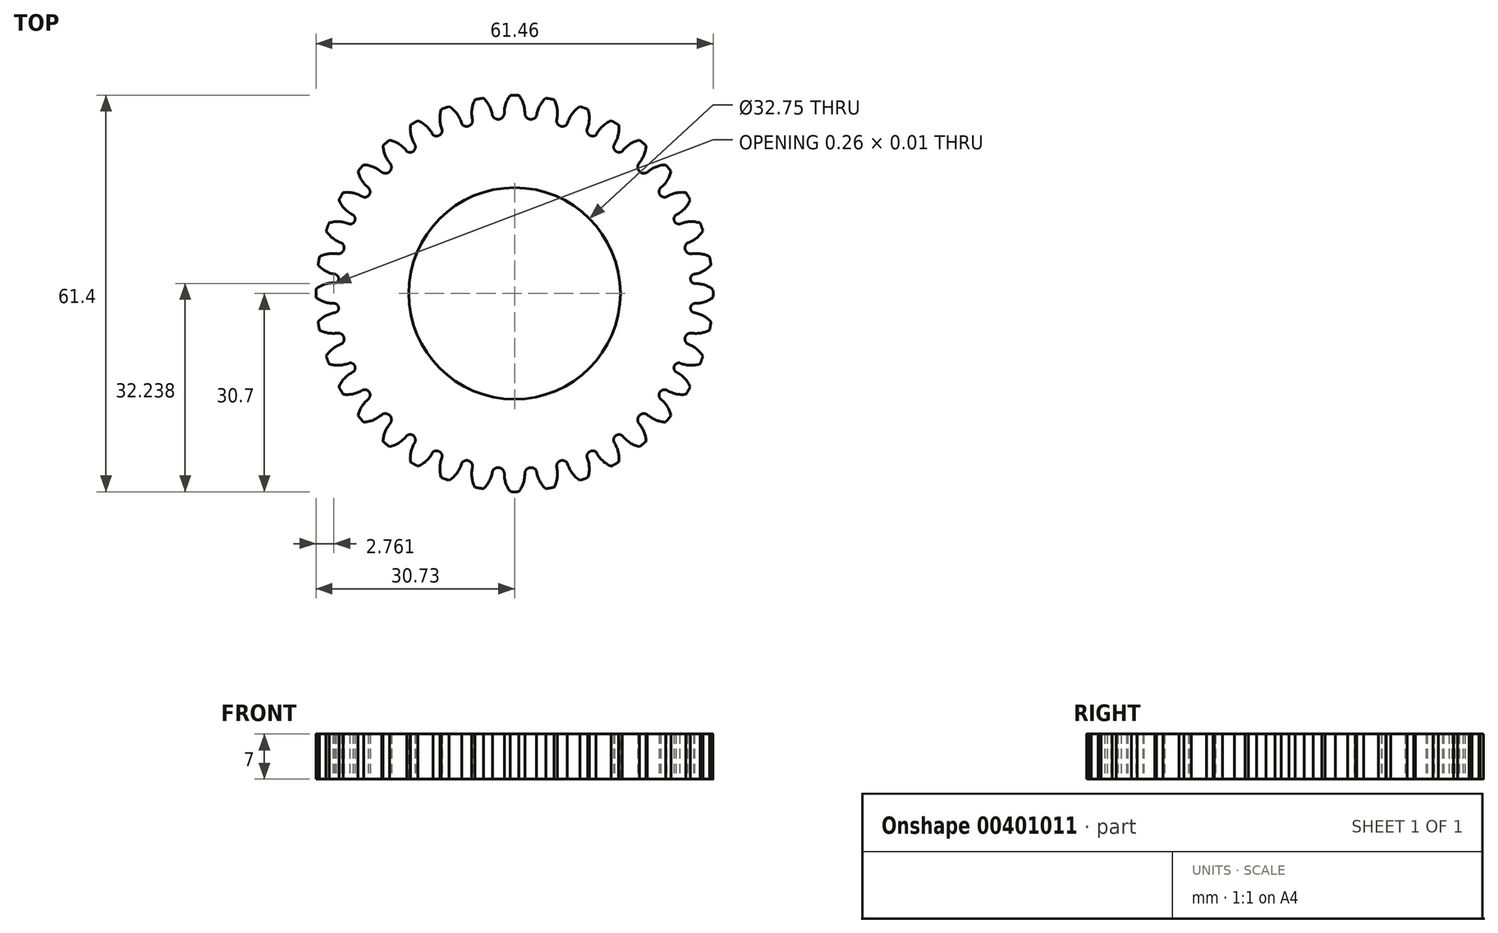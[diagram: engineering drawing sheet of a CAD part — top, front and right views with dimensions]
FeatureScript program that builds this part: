
annotation { "Feature Type Name" : "Feature", "Feature Type Description" : "" }
export const myFeature = defineFeature(function(context is Context, id is Id, definition is map)
    precondition{}
    {
        {
            var Q0;
            Q0=qCreatedBy(makeId("Top.planeOp"),FACE);
            var sketch = newSketch(context, id + "F0", { "sketchPlane" : qUnion([Q0])});
            skArc(sketch, "E0", {"start": v(0.66, 30.69) * mm, "mid": v(0, 30.7) * mm, "end": v(-0.66, 30.69) * mm});
            skLineSegment(sketch, "E1", {"start": v(-1.54, 28.62) * mm, "end": v(-0.66, 30.69) * mm, "construction": true});
            skArc(sketch, "E2", {"start": v(-0.66, 30.69) * mm, "mid": v(-1.56, 28.5) * mm, "end": v(-1.2, 26.14) * mm});
            skArc(sketch, "E3", {"start": v(1.2, 26.14) * mm, "mid": v(1.56, 28.5) * mm, "end": v(0.66, 30.69) * mm});
            skLineSegment(sketch, "E4.MirrorCS", {"start": v(-1.54, -28.62) * mm, "end": v(-0.66, -30.69) * mm, "construction": true});
            skArc(sketch, "E5.MirrorCS", {"start": v(1.2, -26.14) * mm, "mid": v(1.56, -28.5) * mm, "end": v(0.66, -30.69) * mm});
            skArc(sketch, "E6.MirrorCS", {"start": v(0.66, -30.69) * mm, "mid": v(0, -30.7) * mm, "end": v(-0.66, -30.69) * mm});
            skArc(sketch, "E7.MirrorCS", {"start": v(-0.66, -30.69) * mm, "mid": v(-1.56, -28.5) * mm, "end": v(-1.2, -26.14) * mm});
            skArc(sketch, "E8", {"start": v(-30.72, 0.61) * mm, "mid": v(-30.73, -0.05) * mm, "end": v(-30.72, -0.7) * mm});
            skLineSegment(sketch, "E9", {"start": v(-28.65, -1.58) * mm, "end": v(-30.72, -0.7) * mm, "construction": true});
            skArc(sketch, "E10", {"start": v(-28.65, -1.58) * mm, "mid": v(-28.14, -1.63) * mm, "end": v(-27.62, -1.62) * mm});
            skArc(sketch, "E11", {"start": v(-27.84, 1.54) * mm, "mid": v(-29.36, 1.33) * mm, "end": v(-30.72, 0.61) * mm});
            skLineSegment(sketch, "E12", {"start": v(-1.54, 28.62) * mm, "end": v(-3.55, 28.42) * mm, "construction": true});
            skArc(sketch, "E13", {"start": v(-4.83, 30.23) * mm, "mid": v(-5.48, 30.13) * mm, "end": v(-6.13, 30) * mm});
            skLineSegment(sketch, "E14", {"start": v(-6.64, 27.81) * mm, "end": v(-6.13, 30) * mm, "construction": true});
            skArc(sketch, "E15", {"start": v(-6.13, 30) * mm, "mid": v(-6.63, 27.68) * mm, "end": v(-5.88, 25.43) * mm});
            skArc(sketch, "E16", {"start": v(-3.5, 25.85) * mm, "mid": v(-3.56, 28.22) * mm, "end": v(-4.83, 30.23) * mm});
            skArc(sketch, "E17", {"start": v(-10.12, 28.94) * mm, "mid": v(-10.74, 28.73) * mm, "end": v(-11.35, 28.5) * mm});
            skLineSegment(sketch, "E18", {"start": v(-11.48, 26.25) * mm, "end": v(-11.35, 28.5) * mm, "construction": true});
            skArc(sketch, "E19", {"start": v(-11.35, 28.5) * mm, "mid": v(-11.45, 26.12) * mm, "end": v(-10.32, 24.03) * mm});
            skArc(sketch, "E20", {"start": v(-8.05, 24.86) * mm, "mid": v(-8.52, 27.19) * mm, "end": v(-10.12, 28.94) * mm});
            skArc(sketch, "E21", {"start": v(-14.96, 26.75) * mm, "mid": v(-15.54, 26.43) * mm, "end": v(-16.1, 26.09) * mm});
            skLineSegment(sketch, "E22", {"start": v(-15.83, 23.86) * mm, "end": v(-16.1, 26.09) * mm, "construction": true});
            skArc(sketch, "E23", {"start": v(-16.1, 26.09) * mm, "mid": v(-15.78, 23.74) * mm, "end": v(-14.3, 21.88) * mm});
            skArc(sketch, "E24", {"start": v(-12.2, 23.09) * mm, "mid": v(-13.08, 25.3) * mm, "end": v(-14.96, 26.75) * mm});
            skArc(sketch, "E25", {"start": v(-19.34, 23.74) * mm, "mid": v(-19.85, 23.33) * mm, "end": v(-20.35, 22.9) * mm});
            skLineSegment(sketch, "E26", {"start": v(-19.7, 20.75) * mm, "end": v(-20.35, 22.9) * mm, "construction": true});
            skArc(sketch, "E27", {"start": v(-20.35, 22.9) * mm, "mid": v(-19.62, 20.64) * mm, "end": v(-17.85, 19.06) * mm});
            skArc(sketch, "E28", {"start": v(-16, 20.61) * mm, "mid": v(-17.24, 22.64) * mm, "end": v(-19.34, 23.74) * mm});
            skArc(sketch, "E29", {"start": v(-23.36, 19.91) * mm, "mid": v(-23.8, 19.42) * mm, "end": v(-24.2, 18.9) * mm});
            skLineSegment(sketch, "E30", {"start": v(-23.2, 16.9) * mm, "end": v(-24.2, 18.9) * mm, "construction": true});
            skArc(sketch, "E31", {"start": v(-24.2, 18.9) * mm, "mid": v(-23.64, 17.5) * mm, "end": v(-22.64, 16.37) * mm});
            skArc(sketch, "E32", {"start": v(-19.53, 17.42) * mm, "mid": v(-21.1, 19.2) * mm, "end": v(-23.36, 19.91) * mm});
            skArc(sketch, "E33", {"start": v(-26.52, 15.62) * mm, "mid": v(-26.86, 15.06) * mm, "end": v(-27.18, 14.48) * mm});
            skLineSegment(sketch, "E34", {"start": v(-25.83, 12.68) * mm, "end": v(-27.18, 14.48) * mm, "construction": true});
            skArc(sketch, "E35", {"start": v(-27.18, 14.48) * mm, "mid": v(-26.3, 13.11) * mm, "end": v(-24.98, 12.15) * mm});
            skArc(sketch, "E36", {"start": v(-23.5, 14.94) * mm, "mid": v(-24.95, 15.55) * mm, "end": v(-26.52, 15.62) * mm});
            skArc(sketch, "E37", {"start": v(-28.7, 10.92) * mm, "mid": v(-28.94, 10.3) * mm, "end": v(-29.16, 9.68) * mm});
            skLineSegment(sketch, "E38", {"start": v(-27.52, 8.14) * mm, "end": v(-29.16, 9.68) * mm, "construction": true});
            skArc(sketch, "E39", {"start": v(-29.16, 9.68) * mm, "mid": v(-28.13, 8.55) * mm, "end": v(-26.79, 7.83) * mm});
            skArc(sketch, "E40", {"start": v(-30.18, 5.68) * mm, "mid": v(-30.3, 5.03) * mm, "end": v(-30.4, 4.38) * mm});
            skLineSegment(sketch, "E41", {"start": v(-28.52, 3.16) * mm, "end": v(-30.4, 4.38) * mm, "construction": true});
            skArc(sketch, "E42", {"start": v(-30.4, 4.38) * mm, "mid": v(-28.4, 3.12) * mm, "end": v(-26.02, 3.05) * mm});
            skArc(sketch, "E43", {"start": v(-25.6, 5.43) * mm, "mid": v(-27.86, 6.18) * mm, "end": v(-30.18, 5.68) * mm});
            skArc(sketch, "E44", {"start": v(-28.1, 1.54) * mm, "mid": v(-27.23, 2.21) * mm, "end": v(-27.98, 3.01) * mm});
            skArc(sketch, "E45", {"start": v(-27.43, 6.14) * mm, "mid": v(-26.43, 6.73) * mm, "end": v(-26.79, 7.83) * mm});
            skArc(sketch, "E46", {"start": v(-25.93, 10.9) * mm, "mid": v(-24.76, 11.16) * mm, "end": v(-25.21, 12.27) * mm});
            skArc(sketch, "E47", {"start": v(-23.77, 15.1) * mm, "mid": v(-22.54, 15.2) * mm, "end": v(-22.7, 16.42) * mm});
            skArc(sketch, "E48", {"start": v(-20.72, 18.92) * mm, "mid": v(-19.37, 18.84) * mm, "end": v(-19.3, 20.2) * mm});
            skArc(sketch, "E49", {"start": v(-16.93, 22.32) * mm, "mid": v(-15.79, 21.93) * mm, "end": v(-15.44, 23.08) * mm});
            skArc(sketch, "E50", {"start": v(-12.98, 25.15) * mm, "mid": v(-11.77, 24.42) * mm, "end": v(-11.35, 25.77) * mm});
            skArc(sketch, "E51", {"start": v(-8.33, 26.75) * mm, "mid": v(-7.21, 25.88) * mm, "end": v(-6.57, 27.13) * mm});
            skArc(sketch, "E52", {"start": v(-3.49, 27.95) * mm, "mid": v(-2.54, 26.96) * mm, "end": v(-1.59, 27.95) * mm});
            skArc(sketch, "E53.MirrorCS", {"start": v(4.83, 30.23) * mm, "mid": v(5.48, 30.13) * mm, "end": v(6.13, 30) * mm});
            skArc(sketch, "E54.MirrorCS", {"start": v(20.72, 18.92) * mm, "mid": v(19.37, 18.84) * mm, "end": v(19.3, 20.2) * mm});
            skArc(sketch, "E55.MirrorCS", {"start": v(30.18, 5.68) * mm, "mid": v(30.3, 5.03) * mm, "end": v(30.4, 4.38) * mm});
            skArc(sketch, "E56.MirrorCS", {"start": v(30.72, 0.61) * mm, "mid": v(30.73, -0.05) * mm, "end": v(30.72, -0.7) * mm});
            skLineSegment(sketch, "E57.MirrorCS", {"start": v(25.83, 12.68) * mm, "end": v(27.18, 14.48) * mm, "construction": true});
            skArc(sketch, "E58.MirrorCS", {"start": v(14.96, 26.75) * mm, "mid": v(15.54, 26.43) * mm, "end": v(16.1, 26.09) * mm});
            skArc(sketch, "E59.MirrorCS", {"start": v(23.36, 19.91) * mm, "mid": v(23.8, 19.42) * mm, "end": v(24.2, 18.9) * mm});
            skArc(sketch, "E60.MirrorCS", {"start": v(12.98, 25.15) * mm, "mid": v(11.77, 24.42) * mm, "end": v(11.35, 25.77) * mm});
            skArc(sketch, "E61.MirrorCS", {"start": v(11.35, 28.5) * mm, "mid": v(11.45, 26.12) * mm, "end": v(10.32, 24.03) * mm});
            skLineSegment(sketch, "E62.MirrorCS", {"start": v(11.48, 26.25) * mm, "end": v(11.35, 28.5) * mm, "construction": true});
            skArc(sketch, "E63.MirrorCS", {"start": v(19.34, 23.74) * mm, "mid": v(19.85, 23.33) * mm, "end": v(20.35, 22.9) * mm});
            skArc(sketch, "E64.MirrorCS", {"start": v(28.7, 10.92) * mm, "mid": v(28.94, 10.3) * mm, "end": v(29.16, 9.68) * mm});
            skArc(sketch, "E65.MirrorCS", {"start": v(10.12, 28.94) * mm, "mid": v(10.74, 28.73) * mm, "end": v(11.35, 28.5) * mm});
            skLineSegment(sketch, "E66.MirrorCS", {"start": v(23.2, 16.9) * mm, "end": v(24.2, 18.9) * mm, "construction": true});
            skArc(sketch, "E67.MirrorCS", {"start": v(-0.66, 30.69) * mm, "mid": v(0, 30.7) * mm, "end": v(0.66, 30.69) * mm});
            skArc(sketch, "E68.MirrorCS", {"start": v(26.52, 15.62) * mm, "mid": v(26.86, 15.06) * mm, "end": v(27.18, 14.48) * mm});
            skArc(sketch, "E69.MirrorCS", {"start": v(23.77, 15.1) * mm, "mid": v(22.54, 15.2) * mm, "end": v(22.7, 16.42) * mm});
            skArc(sketch, "E70.MirrorCS", {"start": v(25.6, 5.43) * mm, "mid": v(27.86, 6.18) * mm, "end": v(30.18, 5.68) * mm});
            skArc(sketch, "E71.MirrorCS", {"start": v(6.13, 30) * mm, "mid": v(6.63, 27.74) * mm, "end": v(5.94, 25.52) * mm});
            skArc(sketch, "E72.MirrorCS", {"start": v(27.18, 14.48) * mm, "mid": v(25.73, 12.6) * mm, "end": v(23.52, 11.73) * mm});
            skArc(sketch, "E73.MirrorCS", {"start": v(16, 20.61) * mm, "mid": v(17.24, 22.64) * mm, "end": v(19.34, 23.74) * mm});
            skLineSegment(sketch, "E74.MirrorCS", {"start": v(15.83, 23.86) * mm, "end": v(16.1, 26.09) * mm, "construction": true});
            skArc(sketch, "E75.MirrorCS", {"start": v(3.47, 25.97) * mm, "mid": v(3.58, 28.28) * mm, "end": v(4.83, 30.23) * mm});
            skArc(sketch, "E76.MirrorCS", {"start": v(22.3, 13.82) * mm, "mid": v(24.17, 15.3) * mm, "end": v(26.52, 15.62) * mm});
            skArc(sketch, "E77.MirrorCS", {"start": v(16.93, 22.32) * mm, "mid": v(15.79, 21.93) * mm, "end": v(15.44, 23.08) * mm});
            skArc(sketch, "E78.MirrorCS", {"start": v(16.1, 26.09) * mm, "mid": v(15.78, 23.74) * mm, "end": v(14.3, 21.88) * mm});
            skArc(sketch, "E79.MirrorCS", {"start": v(27.43, 6.14) * mm, "mid": v(26.43, 6.73) * mm, "end": v(26.79, 7.83) * mm});
            skArc(sketch, "E80.MirrorCS", {"start": v(0.66, 30.69) * mm, "mid": v(1.56, 28.5) * mm, "end": v(1.2, 26.14) * mm});
            skLineSegment(sketch, "E81.MirrorCS", {"start": v(28.52, 3.16) * mm, "end": v(30.4, 4.38) * mm, "construction": true});
            skArc(sketch, "E82.MirrorCS", {"start": v(26.17, 1.16) * mm, "mid": v(28.52, 1.51) * mm, "end": v(30.72, 0.61) * mm});
            skArc(sketch, "E83.MirrorCS", {"start": v(19.53, 17.42) * mm, "mid": v(21.1, 19.2) * mm, "end": v(23.36, 19.91) * mm});
            skArc(sketch, "E84.MirrorCS", {"start": v(28.1, 1.54) * mm, "mid": v(27.23, 2.21) * mm, "end": v(27.98, 3.01) * mm});
            skArc(sketch, "E85.MirrorCS", {"start": v(24.2, 18.9) * mm, "mid": v(23.1, 16.8) * mm, "end": v(21.08, 15.56) * mm});
            skArc(sketch, "E86.MirrorCS", {"start": v(3.49, 27.95) * mm, "mid": v(2.54, 26.96) * mm, "end": v(1.59, 27.95) * mm});
            skLineSegment(sketch, "E87.MirrorCS", {"start": v(27.52, 8.14) * mm, "end": v(29.16, 9.68) * mm, "construction": true});
            skLineSegment(sketch, "E88.MirrorCS", {"start": v(19.7, 20.75) * mm, "end": v(20.35, 22.9) * mm, "construction": true});
            skArc(sketch, "E89.MirrorCS", {"start": v(29.16, 9.68) * mm, "mid": v(27.4, 8.08) * mm, "end": v(25.07, 7.6) * mm});
            skArc(sketch, "E90.MirrorCS", {"start": v(8.33, 26.75) * mm, "mid": v(7.21, 25.88) * mm, "end": v(6.57, 27.13) * mm});
            skLineSegment(sketch, "E91.MirrorCS", {"start": v(1.54, 28.62) * mm, "end": v(3.55, 28.42) * mm, "construction": true});
            skLineSegment(sketch, "E92.MirrorCS", {"start": v(1.54, 28.62) * mm, "end": v(0.66, 30.69) * mm, "construction": true});
            skArc(sketch, "E93.MirrorCS", {"start": v(30.4, 4.38) * mm, "mid": v(28.4, 3.12) * mm, "end": v(26.02, 3.05) * mm});
            skArc(sketch, "E94.MirrorCS", {"start": v(12.2, 23.09) * mm, "mid": v(13.08, 25.3) * mm, "end": v(14.96, 26.75) * mm});
            skArc(sketch, "E95.MirrorCS", {"start": v(25.93, 10.9) * mm, "mid": v(24.76, 11.16) * mm, "end": v(25.21, 12.27) * mm});
            skLineSegment(sketch, "E96.MirrorCS", {"start": v(6.64, 27.81) * mm, "end": v(6.13, 30) * mm, "construction": true});
            skArc(sketch, "E97.MirrorCS", {"start": v(24.25, 9.88) * mm, "mid": v(26.33, 11) * mm, "end": v(28.7, 10.92) * mm});
            skArc(sketch, "E98.MirrorCS", {"start": v(8.05, 24.86) * mm, "mid": v(8.52, 27.19) * mm, "end": v(10.12, 28.94) * mm});
            skArc(sketch, "E99.MirrorCS", {"start": v(20.35, 22.9) * mm, "mid": v(19.62, 20.64) * mm, "end": v(17.85, 19.06) * mm});
            skLineSegment(sketch, "E100.MirrorCS", {"start": v(28.65, -1.58) * mm, "end": v(30.72, -0.7) * mm, "construction": true});
            skArc(sketch, "E101.MirrorCS", {"start": v(-1.2, 26.14) * mm, "mid": v(-1.56, 28.5) * mm, "end": v(-0.66, 30.69) * mm});
            skArc(sketch, "E102.MirrorCS", {"start": v(-0.66, -30.69) * mm, "mid": v(0, -30.7) * mm, "end": v(0.66, -30.69) * mm});
            skLineSegment(sketch, "E103.MirrorCS", {"start": v(1.54, -28.62) * mm, "end": v(0.66, -30.69) * mm, "construction": true});
            skArc(sketch, "E104.MirrorCS", {"start": v(-1.2, -26.14) * mm, "mid": v(-1.56, -28.5) * mm, "end": v(-0.66, -30.69) * mm});
            skLineSegment(sketch, "E105.MirrorCS", {"start": v(23.2, -16.9) * mm, "end": v(24.2, -18.9) * mm, "construction": true});
            skLineSegment(sketch, "E106.MirrorCS", {"start": v(-1.54, -28.62) * mm, "end": v(-3.55, -28.42) * mm, "construction": true});
            skArc(sketch, "E107.MirrorCS", {"start": v(-28.7, -10.92) * mm, "mid": v(-28.94, -10.3) * mm, "end": v(-29.16, -9.68) * mm});
            skLineSegment(sketch, "E108.MirrorCS", {"start": v(27.52, -8.14) * mm, "end": v(29.16, -9.68) * mm, "construction": true});
            skArc(sketch, "E109.MirrorCS", {"start": v(-14.96, -26.75) * mm, "mid": v(-15.54, -26.43) * mm, "end": v(-16.1, -26.09) * mm});
            skArc(sketch, "E110.MirrorCS", {"start": v(19.34, -23.74) * mm, "mid": v(19.85, -23.33) * mm, "end": v(20.35, -22.9) * mm});
            skArc(sketch, "E111.MirrorCS", {"start": v(24.2, -18.9) * mm, "mid": v(23.1, -16.8) * mm, "end": v(21.08, -15.56) * mm});
            skArc(sketch, "E112.MirrorCS", {"start": v(26.52, -15.62) * mm, "mid": v(26.86, -15.06) * mm, "end": v(27.18, -14.48) * mm});
            skArc(sketch, "E113.MirrorCS", {"start": v(-3.49, -27.95) * mm, "mid": v(-2.54, -26.96) * mm, "end": v(-1.59, -27.95) * mm});
            skLineSegment(sketch, "E114.MirrorCS", {"start": v(-27.52, -8.14) * mm, "end": v(-29.16, -9.68) * mm, "construction": true});
            skArc(sketch, "E115.MirrorCS", {"start": v(-19.34, -23.74) * mm, "mid": v(-19.85, -23.33) * mm, "end": v(-20.35, -22.9) * mm});
            skLineSegment(sketch, "E116.MirrorCS", {"start": v(1.54, -28.62) * mm, "end": v(3.55, -28.42) * mm, "construction": true});
            skArc(sketch, "E117.MirrorCS", {"start": v(0.66, -30.69) * mm, "mid": v(1.56, -28.5) * mm, "end": v(1.2, -26.14) * mm});
            skArc(sketch, "E118.MirrorCS", {"start": v(30.18, -5.68) * mm, "mid": v(30.3, -5.03) * mm, "end": v(30.4, -4.38) * mm});
            skArc(sketch, "E119.MirrorCS", {"start": v(25.93, -10.9) * mm, "mid": v(24.76, -11.16) * mm, "end": v(25.21, -12.27) * mm});
            skLineSegment(sketch, "E120.MirrorCS", {"start": v(25.83, -12.68) * mm, "end": v(27.18, -14.48) * mm, "construction": true});
            skArc(sketch, "E121.MirrorCS", {"start": v(20.35, -22.9) * mm, "mid": v(19.62, -20.64) * mm, "end": v(17.85, -19.06) * mm});
            skArc(sketch, "E122.MirrorCS", {"start": v(14.96, -26.75) * mm, "mid": v(15.54, -26.43) * mm, "end": v(16.1, -26.09) * mm});
            skArc(sketch, "E123.MirrorCS", {"start": v(10.12, -28.94) * mm, "mid": v(10.74, -28.73) * mm, "end": v(11.35, -28.5) * mm});
            skArc(sketch, "E124.MirrorCS", {"start": v(23.77, -15.1) * mm, "mid": v(22.54, -15.2) * mm, "end": v(22.7, -16.42) * mm});
            skArc(sketch, "E125.MirrorCS", {"start": v(-10.12, -28.94) * mm, "mid": v(-10.74, -28.73) * mm, "end": v(-11.35, -28.5) * mm});
            skArc(sketch, "E126.MirrorCS", {"start": v(-30.72, -0.61) * mm, "mid": v(-30.73, 0.05) * mm, "end": v(-30.72, 0.7) * mm});
            skArc(sketch, "E127.MirrorCS", {"start": v(4.83, -30.23) * mm, "mid": v(5.48, -30.13) * mm, "end": v(6.13, -30) * mm});
            skArc(sketch, "E128.MirrorCS", {"start": v(-4.83, -30.23) * mm, "mid": v(-5.48, -30.13) * mm, "end": v(-6.13, -30) * mm});
            skArc(sketch, "E129.MirrorCS", {"start": v(-29.16, -9.68) * mm, "mid": v(-27.4, -8.08) * mm, "end": v(-25.07, -7.6) * mm});
            skArc(sketch, "E130.MirrorCS", {"start": v(20.72, -18.92) * mm, "mid": v(19.37, -18.84) * mm, "end": v(19.3, -20.2) * mm});
            skLineSegment(sketch, "E131.MirrorCS", {"start": v(-19.7, -20.75) * mm, "end": v(-20.35, -22.9) * mm, "construction": true});
            skArc(sketch, "E132.MirrorCS", {"start": v(-26.52, -15.62) * mm, "mid": v(-26.86, -15.06) * mm, "end": v(-27.18, -14.48) * mm});
            skArc(sketch, "E133.MirrorCS", {"start": v(3.49, -27.95) * mm, "mid": v(2.54, -26.96) * mm, "end": v(1.59, -27.95) * mm});
            skLineSegment(sketch, "E134.MirrorCS", {"start": v(11.48, -26.25) * mm, "end": v(11.35, -28.5) * mm, "construction": true});
            skArc(sketch, "E135.MirrorCS", {"start": v(28.7, -10.92) * mm, "mid": v(28.94, -10.3) * mm, "end": v(29.16, -9.68) * mm});
            skArc(sketch, "E136.MirrorCS", {"start": v(-20.72, -18.92) * mm, "mid": v(-19.37, -18.84) * mm, "end": v(-19.3, -20.2) * mm});
            skArc(sketch, "E137.MirrorCS", {"start": v(-30.18, -5.68) * mm, "mid": v(-30.3, -5.03) * mm, "end": v(-30.4, -4.38) * mm});
            skArc(sketch, "E138.MirrorCS", {"start": v(23.36, -19.91) * mm, "mid": v(23.8, -19.42) * mm, "end": v(24.2, -18.9) * mm});
            skLineSegment(sketch, "E139.MirrorCS", {"start": v(19.7, -20.75) * mm, "end": v(20.35, -22.9) * mm, "construction": true});
            skArc(sketch, "E140.MirrorCS", {"start": v(30.72, -0.61) * mm, "mid": v(30.73, 0.05) * mm, "end": v(30.72, 0.7) * mm});
            skArc(sketch, "E141.MirrorCS", {"start": v(-23.36, -19.91) * mm, "mid": v(-23.8, -19.42) * mm, "end": v(-24.2, -18.9) * mm});
            skArc(sketch, "E142.MirrorCS", {"start": v(-25.93, -10.9) * mm, "mid": v(-24.76, -11.16) * mm, "end": v(-25.21, -12.27) * mm});
            skArc(sketch, "E143.MirrorCS", {"start": v(27.43, -6.14) * mm, "mid": v(26.43, -6.73) * mm, "end": v(26.79, -7.83) * mm});
            skArc(sketch, "E144.MirrorCS", {"start": v(-26.17, -1.16) * mm, "mid": v(-28.52, -1.51) * mm, "end": v(-30.72, -0.61) * mm});
            skArc(sketch, "E145.MirrorCS", {"start": v(-12.98, -25.15) * mm, "mid": v(-11.77, -24.42) * mm, "end": v(-11.35, -25.77) * mm});
            skArc(sketch, "E146.MirrorCS", {"start": v(-12.2, -23.09) * mm, "mid": v(-13.08, -25.3) * mm, "end": v(-14.96, -26.75) * mm});
            skArc(sketch, "E147.MirrorCS", {"start": v(-3.5, -25.85) * mm, "mid": v(-3.56, -28.22) * mm, "end": v(-4.83, -30.23) * mm});
            skArc(sketch, "E148.MirrorCS", {"start": v(-8.33, -26.75) * mm, "mid": v(-7.21, -25.88) * mm, "end": v(-6.57, -27.13) * mm});
            skArc(sketch, "E149.MirrorCS", {"start": v(12.98, -25.15) * mm, "mid": v(11.77, -24.42) * mm, "end": v(11.35, -25.77) * mm});
            skArc(sketch, "E150.MirrorCS", {"start": v(16.93, -22.32) * mm, "mid": v(15.79, -21.93) * mm, "end": v(15.44, -23.08) * mm});
            skArc(sketch, "E151.MirrorCS", {"start": v(8.33, -26.75) * mm, "mid": v(7.21, -25.88) * mm, "end": v(6.57, -27.13) * mm});
            skLineSegment(sketch, "E152.MirrorCS", {"start": v(-25.83, -12.68) * mm, "end": v(-27.18, -14.48) * mm, "construction": true});
            skArc(sketch, "E153.MirrorCS", {"start": v(-23.77, -15.1) * mm, "mid": v(-22.54, -15.2) * mm, "end": v(-22.7, -16.42) * mm});
            skLineSegment(sketch, "E154.MirrorCS", {"start": v(15.83, -23.86) * mm, "end": v(16.1, -26.09) * mm, "construction": true});
            skArc(sketch, "E155.MirrorCS", {"start": v(-11.35, -28.5) * mm, "mid": v(-11.45, -26.12) * mm, "end": v(-10.32, -24.03) * mm});
            skArc(sketch, "E156.MirrorCS", {"start": v(8.05, -24.86) * mm, "mid": v(8.52, -27.19) * mm, "end": v(10.12, -28.94) * mm});
            skArc(sketch, "E157.MirrorCS", {"start": v(-28.1, -1.54) * mm, "mid": v(-27.23, -2.21) * mm, "end": v(-27.98, -3.01) * mm});
            skArc(sketch, "E158.MirrorCS", {"start": v(-8.05, -24.86) * mm, "mid": v(-8.52, -27.19) * mm, "end": v(-10.12, -28.94) * mm});
            skArc(sketch, "E159.MirrorCS", {"start": v(-27.43, -6.14) * mm, "mid": v(-26.43, -6.73) * mm, "end": v(-26.79, -7.83) * mm});
            skArc(sketch, "E160.MirrorCS", {"start": v(-19.53, -17.42) * mm, "mid": v(-21.1, -19.2) * mm, "end": v(-23.36, -19.91) * mm});
            skArc(sketch, "E161.MirrorCS", {"start": v(12.2, -23.09) * mm, "mid": v(13.08, -25.3) * mm, "end": v(14.96, -26.75) * mm});
            skArc(sketch, "E162.MirrorCS", {"start": v(-16, -20.61) * mm, "mid": v(-17.24, -22.64) * mm, "end": v(-19.34, -23.74) * mm});
            skLineSegment(sketch, "E163.MirrorCS", {"start": v(-28.52, -3.16) * mm, "end": v(-30.4, -4.38) * mm, "construction": true});
            skLineSegment(sketch, "E164.MirrorCS", {"start": v(28.52, -3.16) * mm, "end": v(30.4, -4.38) * mm, "construction": true});
            skArc(sketch, "E165.MirrorCS", {"start": v(30.4, -4.38) * mm, "mid": v(28.4, -3.12) * mm, "end": v(26.02, -3.05) * mm});
            skArc(sketch, "E166.MirrorCS", {"start": v(-24.25, -9.88) * mm, "mid": v(-26.33, -11) * mm, "end": v(-28.7, -10.92) * mm});
            skArc(sketch, "E167.MirrorCS", {"start": v(27.18, -14.48) * mm, "mid": v(25.73, -12.6) * mm, "end": v(23.52, -11.73) * mm});
            skArc(sketch, "E168.MirrorCS", {"start": v(3.5, -25.85) * mm, "mid": v(3.56, -28.22) * mm, "end": v(4.83, -30.23) * mm});
            skArc(sketch, "E169.MirrorCS", {"start": v(-30.4, -4.38) * mm, "mid": v(-28.4, -3.12) * mm, "end": v(-26.02, -3.05) * mm});
            skArc(sketch, "E170.MirrorCS", {"start": v(11.35, -28.5) * mm, "mid": v(11.45, -26.12) * mm, "end": v(10.32, -24.03) * mm});
            skLineSegment(sketch, "E171.MirrorCS", {"start": v(-23.2, -16.9) * mm, "end": v(-24.2, -18.9) * mm, "construction": true});
            skArc(sketch, "E172.MirrorCS", {"start": v(-16.93, -22.32) * mm, "mid": v(-15.79, -21.93) * mm, "end": v(-15.44, -23.08) * mm});
            skArc(sketch, "E173.MirrorCS", {"start": v(-22.3, -13.82) * mm, "mid": v(-24.17, -15.3) * mm, "end": v(-26.52, -15.62) * mm});
            skArc(sketch, "E174.MirrorCS", {"start": v(-16.1, -26.09) * mm, "mid": v(-15.78, -23.74) * mm, "end": v(-14.3, -21.88) * mm});
            skArc(sketch, "E175.MirrorCS", {"start": v(29.16, -9.68) * mm, "mid": v(27.4, -8.08) * mm, "end": v(25.07, -7.6) * mm});
            skArc(sketch, "E176.MirrorCS", {"start": v(16.1, -26.09) * mm, "mid": v(15.78, -23.74) * mm, "end": v(14.3, -21.88) * mm});
            skArc(sketch, "E177.MirrorCS", {"start": v(19.53, -17.42) * mm, "mid": v(21.1, -19.2) * mm, "end": v(23.36, -19.91) * mm});
            skLineSegment(sketch, "E178.MirrorCS", {"start": v(6.64, -27.81) * mm, "end": v(6.13, -30) * mm, "construction": true});
            skArc(sketch, "E179.MirrorCS", {"start": v(25.6, -5.43) * mm, "mid": v(27.86, -6.18) * mm, "end": v(30.18, -5.68) * mm});
            skArc(sketch, "E180.MirrorCS", {"start": v(-20.35, -22.9) * mm, "mid": v(-19.62, -20.64) * mm, "end": v(-17.85, -19.06) * mm});
            skLineSegment(sketch, "E181.MirrorCS", {"start": v(-11.48, -26.25) * mm, "end": v(-11.35, -28.5) * mm, "construction": true});
            skArc(sketch, "E182.MirrorCS", {"start": v(-25.6, -5.43) * mm, "mid": v(-27.86, -6.18) * mm, "end": v(-30.18, -5.68) * mm});
            skArc(sketch, "E183.MirrorCS", {"start": v(-24.2, -18.9) * mm, "mid": v(-23.1, -16.8) * mm, "end": v(-21.08, -15.56) * mm});
            skArc(sketch, "E184.MirrorCS", {"start": v(22.3, -13.82) * mm, "mid": v(24.17, -15.3) * mm, "end": v(26.52, -15.62) * mm});
            skArc(sketch, "E185.MirrorCS", {"start": v(26.18, 1.17) * mm, "mid": v(26.18, 1.21) * mm, "end": v(26.17, 1.25) * mm});
            skArc(sketch, "E186.MirrorCS", {"start": v(24.25, -9.88) * mm, "mid": v(26.33, -11) * mm, "end": v(28.7, -10.92) * mm});
            skArc(sketch, "E187.MirrorCS", {"start": v(26.17, -1.16) * mm, "mid": v(28.52, -1.51) * mm, "end": v(30.72, -0.61) * mm});
            skArc(sketch, "E188.MirrorCS", {"start": v(-27.18, -14.48) * mm, "mid": v(-25.73, -12.6) * mm, "end": v(-23.52, -11.73) * mm});
            skArc(sketch, "E189.MirrorCS", {"start": v(16, -20.61) * mm, "mid": v(17.24, -22.64) * mm, "end": v(19.34, -23.74) * mm});
            skLineSegment(sketch, "E190.MirrorCS", {"start": v(-15.83, -23.86) * mm, "end": v(-16.1, -26.09) * mm, "construction": true});
            skArc(sketch, "E191.MirrorCS", {"start": v(6.13, -30) * mm, "mid": v(6.63, -27.68) * mm, "end": v(5.88, -25.43) * mm});
            skArc(sketch, "E192.MirrorCS", {"start": v(28.1, -1.54) * mm, "mid": v(27.23, -2.21) * mm, "end": v(27.98, -3.01) * mm});
            skLineSegment(sketch, "E193.MirrorCS", {"start": v(-6.64, -27.81) * mm, "end": v(-6.13, -30) * mm, "construction": true});
            skLineSegment(sketch, "E194.MirrorCS", {"start": v(-28.65, 1.58) * mm, "end": v(-29.05, 1.42) * mm, "construction": true});
            skLineSegment(sketch, "E195.MirrorCS", {"start": v(28.65, 1.58) * mm, "end": v(30.72, 0.7) * mm, "construction": true});
            skArc(sketch, "E196.MirrorCS", {"start": v(-30.72, 0.7) * mm, "mid": v(-28.52, 1.6) * mm, "end": v(-26.17, 1.25) * mm});
            skArc(sketch, "E197.MirrorCS", {"start": v(-6.13, -30) * mm, "mid": v(-6.63, -27.68) * mm, "end": v(-5.88, -25.43) * mm});
            skPoint(sketch, "E198.orphan", {"position": v(3.5, 25.85) * mm});
            skPoint(sketch, "E199.orphan", {"position": v(5.88, 25.43) * mm});
            skLineSegment(sketch, "E200", {"start": v(-23.52, -11.73) * mm, "end": v(-23.43, -11.72) * mm});
            skArc(sketch, "E201.trimOffspring", {"start": v(-25.53, 10.74) * mm, "mid": v(-27.1, 11.12) * mm, "end": v(-28.7, 10.92) * mm});
            skPoint(sketch, "E202.end.orphan", {"position": v(-23.52, 11.73) * mm});
            skPoint(sketch, "E203.orphan", {"position": v(-22.3, 13.82) * mm});
            skPoint(sketch, "E204.start.orphan", {"position": v(-24.25, 9.88) * mm});
            skPoint(sketch, "E205.orphan", {"position": v(-25.07, 7.6) * mm});
            skArc(sketch, "E206.trimOffspring", {"start": v(-26.18, -1.17) * mm, "mid": v(-26.18, -1.21) * mm, "end": v(-26.17, -1.25) * mm});
            skArc(sketch, "E207.trimOffspring", {"start": v(26.18, -1.17) * mm, "mid": v(26.18, -1.21) * mm, "end": v(26.17, -1.25) * mm});
            skPoint(sketch, "E208.end.orphan", {"position": v(-21.08, 15.56) * mm});
            skPoint(sketch, "E209.orphan", {"position": v(-26.17, 1.16) * mm});
            skLineSegment(sketch, "E210.trimOffspring", {"start": v(-30.39, 0.84) * mm, "end": v(-30.72, 0.7) * mm, "construction": true});
            skSolve(sketch);
        }
        {
            var Q0;
            Q0 = qSketchRegion(id + "F0", true);
            extrude(context, id + "F1", {"entities" : qUnion([Q0]), "depth" : 7 * mm});
        }
        {
            var Q0;
            Q0=makeQuery(id+"F1.opExtrude","CAP_FACE",FACE,{"disambiguationData":[OSD([sQuery(id+"F0.wireOp",EDGE,"E11"),sQuery(id+"F0.wireOp",EDGE,"E13"),sQuery(id+"F0.wireOp",EDGE,"E15"),sQuery(id+"F0.wireOp",EDGE,"E16"),sQuery(id+"F0.wireOp",EDGE,"E17"),sQuery(id+"F0.wireOp",EDGE,"E19"),sQuery(id+"F0.wireOp",EDGE,"E20"),sQuery(id+"F0.wireOp",EDGE,"E21"),sQuery(id+"F0.wireOp",EDGE,"E23"),sQuery(id+"F0.wireOp",EDGE,"E24"),sQuery(id+"F0.wireOp",EDGE,"E25"),sQuery(id+"F0.wireOp",EDGE,"E27"),sQuery(id+"F0.wireOp",EDGE,"E28"),sQuery(id+"F0.wireOp",EDGE,"E29"),sQuery(id+"F0.wireOp",EDGE,"E31"),sQuery(id+"F0.wireOp",EDGE,"E32"),sQuery(id+"F0.wireOp",EDGE,"E33"),sQuery(id+"F0.wireOp",EDGE,"E35"),sQuery(id+"F0.wireOp",EDGE,"E36"),sQuery(id+"F0.wireOp",EDGE,"E37"),sQuery(id+"F0.wireOp",EDGE,"E39"),sQuery(id+"F0.wireOp",EDGE,"E40"),sQuery(id+"F0.wireOp",EDGE,"E42"),sQuery(id+"F0.wireOp",EDGE,"E43"),sQuery(id+"F0.wireOp",EDGE,"E44"),sQuery(id+"F0.wireOp",EDGE,"E45"),sQuery(id+"F0.wireOp",EDGE,"E46"),sQuery(id+"F0.wireOp",EDGE,"E47"),sQuery(id+"F0.wireOp",EDGE,"E48"),sQuery(id+"F0.wireOp",EDGE,"E49"),sQuery(id+"F0.wireOp",EDGE,"E50"),sQuery(id+"F0.wireOp",EDGE,"E51"),sQuery(id+"F0.wireOp",EDGE,"E52"),sQuery(id+"F0.wireOp",EDGE,"E53.MirrorCS"),sQuery(id+"F0.wireOp",EDGE,"E54.MirrorCS"),sQuery(id+"F0.wireOp",EDGE,"E55.MirrorCS"),sQuery(id+"F0.wireOp",EDGE,"E56.MirrorCS"),sQuery(id+"F0.wireOp",EDGE,"E58.MirrorCS"),sQuery(id+"F0.wireOp",EDGE,"E59.MirrorCS"),sQuery(id+"F0.wireOp",EDGE,"E60.MirrorCS"),sQuery(id+"F0.wireOp",EDGE,"E61.MirrorCS"),sQuery(id+"F0.wireOp",EDGE,"E63.MirrorCS"),sQuery(id+"F0.wireOp",EDGE,"E64.MirrorCS"),sQuery(id+"F0.wireOp",EDGE,"E65.MirrorCS"),sQuery(id+"F0.wireOp",EDGE,"E67.MirrorCS"),sQuery(id+"F0.wireOp",EDGE,"E68.MirrorCS"),sQuery(id+"F0.wireOp",EDGE,"E69.MirrorCS"),sQuery(id+"F0.wireOp",EDGE,"E70.MirrorCS"),sQuery(id+"F0.wireOp",EDGE,"E71.MirrorCS"),sQuery(id+"F0.wireOp",EDGE,"E72.MirrorCS"),sQuery(id+"F0.wireOp",EDGE,"E73.MirrorCS"),sQuery(id+"F0.wireOp",EDGE,"E75.MirrorCS"),sQuery(id+"F0.wireOp",EDGE,"E76.MirrorCS"),sQuery(id+"F0.wireOp",EDGE,"E77.MirrorCS"),sQuery(id+"F0.wireOp",EDGE,"E78.MirrorCS"),sQuery(id+"F0.wireOp",EDGE,"E79.MirrorCS"),sQuery(id+"F0.wireOp",EDGE,"E80.MirrorCS"),sQuery(id+"F0.wireOp",EDGE,"E82.MirrorCS"),sQuery(id+"F0.wireOp",EDGE,"E83.MirrorCS"),sQuery(id+"F0.wireOp",EDGE,"E84.MirrorCS"),sQuery(id+"F0.wireOp",EDGE,"E85.MirrorCS"),sQuery(id+"F0.wireOp",EDGE,"E86.MirrorCS"),sQuery(id+"F0.wireOp",EDGE,"E89.MirrorCS"),sQuery(id+"F0.wireOp",EDGE,"E90.MirrorCS"),sQuery(id+"F0.wireOp",EDGE,"E93.MirrorCS"),sQuery(id+"F0.wireOp",EDGE,"E94.MirrorCS"),sQuery(id+"F0.wireOp",EDGE,"E95.MirrorCS"),sQuery(id+"F0.wireOp",EDGE,"E97.MirrorCS"),sQuery(id+"F0.wireOp",EDGE,"E98.MirrorCS"),sQuery(id+"F0.wireOp",EDGE,"E99.MirrorCS"),sQuery(id+"F0.wireOp",EDGE,"E101.MirrorCS"),sQuery(id+"F0.wireOp",EDGE,"E102.MirrorCS"),sQuery(id+"F0.wireOp",EDGE,"E107.MirrorCS"),sQuery(id+"F0.wireOp",EDGE,"E109.MirrorCS"),sQuery(id+"F0.wireOp",EDGE,"E110.MirrorCS"),sQuery(id+"F0.wireOp",EDGE,"E111.MirrorCS"),sQuery(id+"F0.wireOp",EDGE,"E112.MirrorCS"),sQuery(id+"F0.wireOp",EDGE,"E113.MirrorCS"),sQuery(id+"F0.wireOp",EDGE,"E115.MirrorCS"),sQuery(id+"F0.wireOp",EDGE,"E117.MirrorCS"),sQuery(id+"F0.wireOp",EDGE,"E118.MirrorCS"),sQuery(id+"F0.wireOp",EDGE,"E119.MirrorCS"),sQuery(id+"F0.wireOp",EDGE,"E7.MirrorCS"),sQuery(id+"F0.wireOp",EDGE,"E121.MirrorCS"),sQuery(id+"F0.wireOp",EDGE,"E122.MirrorCS"),sQuery(id+"F0.wireOp",EDGE,"E123.MirrorCS"),sQuery(id+"F0.wireOp",EDGE,"E124.MirrorCS"),sQuery(id+"F0.wireOp",EDGE,"E125.MirrorCS"),sQuery(id+"F0.wireOp",EDGE,"E126.MirrorCS"),sQuery(id+"F0.wireOp",EDGE,"E127.MirrorCS"),sQuery(id+"F0.wireOp",EDGE,"E128.MirrorCS"),sQuery(id+"F0.wireOp",EDGE,"E129.MirrorCS"),sQuery(id+"F0.wireOp",EDGE,"E130.MirrorCS"),sQuery(id+"F0.wireOp",EDGE,"E132.MirrorCS"),sQuery(id+"F0.wireOp",EDGE,"E133.MirrorCS"),sQuery(id+"F0.wireOp",EDGE,"E135.MirrorCS"),sQuery(id+"F0.wireOp",EDGE,"E136.MirrorCS"),sQuery(id+"F0.wireOp",EDGE,"E137.MirrorCS"),sQuery(id+"F0.wireOp",EDGE,"E138.MirrorCS"),sQuery(id+"F0.wireOp",EDGE,"E140.MirrorCS"),sQuery(id+"F0.wireOp",EDGE,"E141.MirrorCS"),sQuery(id+"F0.wireOp",EDGE,"E142.MirrorCS"),sQuery(id+"F0.wireOp",EDGE,"E143.MirrorCS"),sQuery(id+"F0.wireOp",EDGE,"E144.MirrorCS"),sQuery(id+"F0.wireOp",EDGE,"E145.MirrorCS"),sQuery(id+"F0.wireOp",EDGE,"E146.MirrorCS"),sQuery(id+"F0.wireOp",EDGE,"E147.MirrorCS"),sQuery(id+"F0.wireOp",EDGE,"E148.MirrorCS"),sQuery(id+"F0.wireOp",EDGE,"E149.MirrorCS"),sQuery(id+"F0.wireOp",EDGE,"E150.MirrorCS"),sQuery(id+"F0.wireOp",EDGE,"E151.MirrorCS"),sQuery(id+"F0.wireOp",EDGE,"E153.MirrorCS"),sQuery(id+"F0.wireOp",EDGE,"E155.MirrorCS"),sQuery(id+"F0.wireOp",EDGE,"E156.MirrorCS"),sQuery(id+"F0.wireOp",EDGE,"E157.MirrorCS"),sQuery(id+"F0.wireOp",EDGE,"E158.MirrorCS"),sQuery(id+"F0.wireOp",EDGE,"E159.MirrorCS"),sQuery(id+"F0.wireOp",EDGE,"E160.MirrorCS"),sQuery(id+"F0.wireOp",EDGE,"E161.MirrorCS"),sQuery(id+"F0.wireOp",EDGE,"E162.MirrorCS"),sQuery(id+"F0.wireOp",EDGE,"E165.MirrorCS"),sQuery(id+"F0.wireOp",EDGE,"E166.MirrorCS"),sQuery(id+"F0.wireOp",EDGE,"E167.MirrorCS"),sQuery(id+"F0.wireOp",EDGE,"E168.MirrorCS"),sQuery(id+"F0.wireOp",EDGE,"E169.MirrorCS"),sQuery(id+"F0.wireOp",EDGE,"E170.MirrorCS"),sQuery(id+"F0.wireOp",EDGE,"E172.MirrorCS"),sQuery(id+"F0.wireOp",EDGE,"E173.MirrorCS"),sQuery(id+"F0.wireOp",EDGE,"E174.MirrorCS"),sQuery(id+"F0.wireOp",EDGE,"E175.MirrorCS"),sQuery(id+"F0.wireOp",EDGE,"E176.MirrorCS"),sQuery(id+"F0.wireOp",EDGE,"E177.MirrorCS"),sQuery(id+"F0.wireOp",EDGE,"E179.MirrorCS"),sQuery(id+"F0.wireOp",EDGE,"E180.MirrorCS"),sQuery(id+"F0.wireOp",EDGE,"E182.MirrorCS"),sQuery(id+"F0.wireOp",EDGE,"E183.MirrorCS"),sQuery(id+"F0.wireOp",EDGE,"E184.MirrorCS"),sQuery(id+"F0.wireOp",EDGE,"E186.MirrorCS"),sQuery(id+"F0.wireOp",EDGE,"E187.MirrorCS"),sQuery(id+"F0.wireOp",EDGE,"E188.MirrorCS"),sQuery(id+"F0.wireOp",EDGE,"E189.MirrorCS"),sQuery(id+"F0.wireOp",EDGE,"E191.MirrorCS"),sQuery(id+"F0.wireOp",EDGE,"E192.MirrorCS"),sQuery(id+"F0.wireOp",EDGE,"E196.MirrorCS"),sQuery(id+"F0.wireOp",EDGE,"E197.MirrorCS"),sQuery(id+"F0.wireOp",EDGE,"E201.trimOffspring")])],"isStart":false});
            var sketch = newSketch(context, id + "F2", { "sketchPlane" : qUnion([Q0])});
            skCircle(sketch, "E211", {"center": v(0, 0) * mm, "radius": 16.38 * mm});
            skSolve(sketch);
        }
        {
            var Q0;
            Q0 = qSketchRegion(id + "F2", true);
            extrude(context, id + "F3", {"entities" : qUnion([Q0]), "operationType" : NewBodyOperationType.REMOVE, "oppositeDirection" : true, "depth" : 25 * mm});
        }
    });
